# Revit family: LAMP_KOMBIC 100 ROUND IP55 CRI80 OPAL
name_source: partatom
category: Luminarias
revit_build: Autodesk Revit 2018 (Build: 20190510_1515(x64)
units: mm (PartAtom-declared; Revit-internal decimal feet)

## family parameters
Anfitrión = Cara
Compartido = No
Corte con vacíos al cargar = No
Cota de conector redondo = Diámetro de uso
Origen de luz = Sí
Punto de cálculo de habitación = No
Tipo de pieza = Normal

## types (8) — shared parameters
CRI = 80
Cambio de temperatura de color de luz atenuada = <Ninguno>
Diameter = 99 mm  [stored 0.324803 ft]
Elevación por defecto = 1219 mm
Fabricante = LAMP
Filtro de color = 16777215
Finish = Shiny white RAL 9010
Gear = Electronic
Height = 75 mm
IEE = A+
Installation instructions = https://www.lamp.es
Insulation class = II
LED Lifetime = 50.000 L80 B10
Lamp = COB LED
Last update = 13/07/2021
Luminaire type = Downlight
MacAdam = 3
Manufacturer URL = http://www.lamp.es
Manufacturer country = Spain
Manufacturer name = LAMP
Material aro = LAMP_Plástico genérico BL
Material difusor = LAMP_PMMA Difusor Kombic
Material disipador = LAMP_Aluminio Disipador Kombic
Material reflector = LAMP_PC Reflector Kombic Metalizado Mate
Power Supply = 220-240V 50/60Hz
Product URL = https://www.lamp.es
Product datasheet = http://www.lamp.es
Protection rating = IP55
Recessed diameter = 95 mm
Type = COB PHILIPS
Weight = 0.52 kg
Ángulo de inclinación = -90.00°

## per-type parameters (varying)
| type | Archivo de red fotométrica | Efficacy | Modelo | Plum | Power | Product code |
| 1392LM 3000K DALI M/W | K11RD2055OP830nMW.IES | 104 lm/W | K11RD2055OP830DMW | 13 W | 12 W | K11RD2055OP830DMW |
| 1392LM 3000K  M/W | K11RD2055OP830NMW.IES | 104 lm/W | K11RD2055OP830NMW | 13 W | 12 W | K11RD2055OP830NMW |
| 1474LM 4000K DALI M/W | K11RD2055OP840nMW.IES | 110 lm/W | K11RD2055OP840DMW | 13 W | 12 W | K11RD2055OP840DMW |
| 1474LM 4000K  M/W | K11RD2055OP840NMW.IES | 110 lm/W | K11RD2055OP840NMW | 13 W | 12 W | K11RD2055OP840NMW |
| 1867LM 3000K DALI M/W | K11RD2555OP830nMW.IES | 98 lm/W | K11RD2555OP830DMW | 19 W | 17 W | K11RD2555OP830DMW |
| 1867LM 3000K  M/W | K11RD2555OP830NMW.IES | 98 lm/W | K11RD2555OP830NMW | 19 W | 17 W | K11RD2555OP830NMW |
| 1978LM 4000K DALI M/W | K11RD2555OP840nMW.IES | 104 lm/W | K11RD2555OP840DMW | 19 W | 17 W | K11RD2555OP840DMW |
| 1978LM 4000K  M/W | K11RD2555OP840NMW.IES | 104 lm/W | K11RD2555OP840NMW | 19 W | 17 W | K11RD2555OP840NMW |

note: [stored X ft] marks values corroborated as IEEE doubles in the binary element streams (Revit-internal decimal feet)
